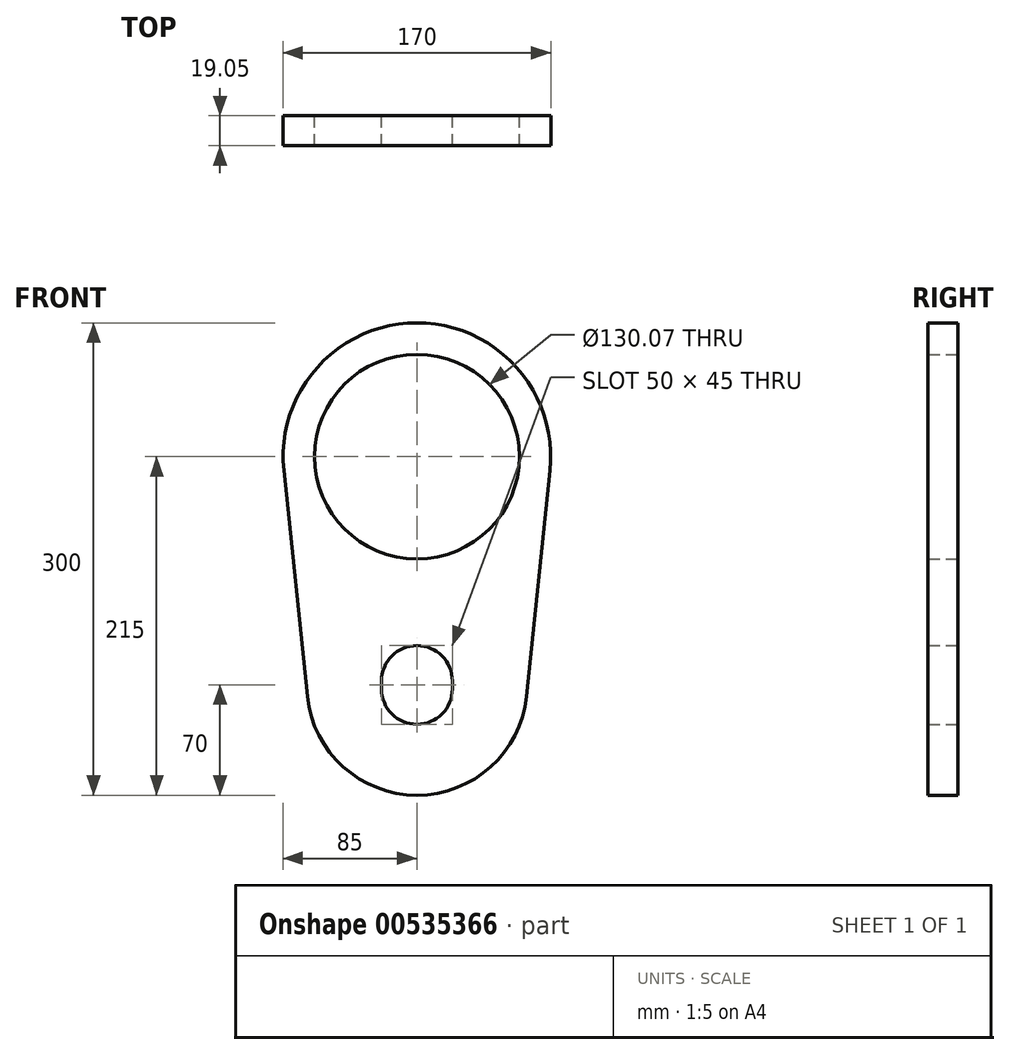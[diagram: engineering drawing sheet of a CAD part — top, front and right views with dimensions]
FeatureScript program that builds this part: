
annotation { "Feature Type Name" : "Feature", "Feature Type Description" : "" }
export const myFeature = defineFeature(function(context is Context, id is Id, definition is map)
    precondition{}
    {
        {
            var Q0;
            Q0=qCreatedBy(makeId("Front.planeOp"),FACE);
            var sketch = newSketch(context, id + "F0", { "sketchPlane" : qUnion([Q0])});
            skArc(sketch, "E0", {"start": v(84.54, -8.8) * mm, "mid": v(0, 85) * mm, "end": v(-84.54, -8.8) * mm});
            skLineSegment(sketch, "E1", {"start": v(-84.54, -8.8) * mm, "end": v(-69.62, -152.24) * mm});
            skLineSegment(sketch, "E2", {"start": v(0, 0) * mm, "end": v(0, -145) * mm, "construction": true});
            skLineSegment(sketch, "E3.MirrorCS", {"start": v(84.54, -8.8) * mm, "end": v(69.62, -152.24) * mm});
            skArc(sketch, "E4.trimOffspring", {"start": v(-69.62, -152.24) * mm, "mid": v(0, -215) * mm, "end": v(69.62, -152.24) * mm});
            skCircle(sketch, "E5", {"center": v(0, 0) * mm, "radius": 65.04 * mm});
            skLineSegment(sketch, "E6", {"start": v(0, -142.5) * mm, "end": v(0, -147.5) * mm});
            skArc(sketch, "E7.0.startCap", {"start": v(-22.5, -142.5) * mm, "mid": v(0, -120) * mm, "end": v(22.5, -142.5) * mm});
            skArc(sketch, "E7.0.endCap", {"start": v(22.5, -147.5) * mm, "mid": v(0, -170) * mm, "end": v(-22.5, -147.5) * mm});
            skLineSegment(sketch, "E7.0.left", {"start": v(22.5, -142.5) * mm, "end": v(22.5, -147.5) * mm});
            skLineSegment(sketch, "E7.0.right", {"start": v(-22.5, -142.5) * mm, "end": v(-22.5, -147.5) * mm});
            skSolve(sketch);
        }
        {
            var Q0;
            Q0=qSketchRegion(id+"F0",true);
            extrude(context, id + "F1", {"entities" : qUnion([Q0]), "depth" : 19.05 * mm, "offsetDistance" : 25.4 * mm});
        }
    });
